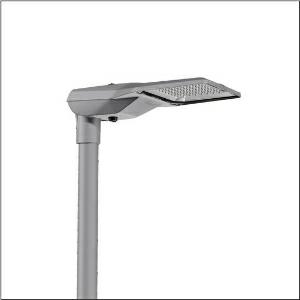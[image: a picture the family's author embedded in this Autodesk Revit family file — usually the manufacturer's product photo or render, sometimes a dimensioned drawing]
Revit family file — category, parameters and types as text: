
# Revit family: streetlight_sl_21_midi___st1_0a_5xe3d33t08mb_6958
name_source: partatom
category: Lighting Fixtures
units: mm (PartAtom-declared; Revit-internal decimal feet)

## family parameters
Cut with Voids When Loaded = No
Host = Face
Light Source = No
Part Type = Normal
Room Calculation Point = No
Round Connector Dimension = Use Diameter
Shared = No

## types (1)
- --- (1 x LED, 18270 lm, 136 W, 3000K)
    Apparent Load = 136 VA
    CIE Flux Codes = 37 72 97 100 100
    Color Rendering = 70
    Color Temperature = 3000K
    Default Elevation = 1800 mm
    Description = Streetlight SL 21 midi, mast luminaire, primary light control with lens, of PMMA, primary optical cover: cover, of toughened safety glass, transparent, light distribution: ST1.0a, light emission: direct distribution, primary light characteristic: asymmetric, installation type: side-entry, post-top, LED, High Power LED, rated luminous flux: 18.270lm, luminous efficacy: 134lm/W, light colour: 730, colour temperature: 3000K, control gear: D4i, control: flexible luminous flux parameterisation, time-dependent luminous flux control, constant luminous flux control, overheat protection, pre-setting: logarithmic dimming characteristic, mains connection: 230..240V, AC, 50/60Hz, start of lifetime: 136W, end of service life: 142W, reduction: 61W, luminaire housing, of diecast aluminium, powder-coated, Siteco® metallic grey (DB 702S), corrosivity category C5 mid according to DIN EN ISO 12944, please order mast flange separately, inclination adjustable: 0°, 5°, 10°, 15°, sealing non-destructively replaceable, multi-level sealing system, length: 644mm, width: 335mm, height: 110mm, mast flange for spigot size: 42mm (side-entry): 5XC10008XM4, 60/48mm (side-entry/post-top): 5XC10108XM2, 76/60mm (side-entry/post-top): 5XC10108XM1, mounting height: 4..8m, Smart Interface below and above, protection rating (complete): IP66, insulation class (complete): insulation class II (safety insulation), certification: CE, ENEC, ENEC+, VDE, impact resistance: IK10, permissible operating ambient temperature for outdoor applications: -40..+50°C, standard-compliant lighting for roads and squares, packaging unit: 1 piece

Light Distribution: ST1.0a
    Height = 111 mm
    Lamp = 1 x LED
    Lamp Light Flux = 18270 lm
    Lamp Power = 136 W
    Lamp count = 1
    Length = 644 mm
    Luminous efficacy = 134 lm/W
    Manufacturer = Siteco
    ModVariant = No
    Model = 5XE3D33T08MB
    Number of Poles = 1
    OnlyDefault = Yes
    Power Factor = 1
    Product Name = Streetlight SL 21 midi | ST1.0a
    Product group = mast luminaire | pylon top
    ProductGroupID = 6100
    Protection Class = Protection class II
    Protection Degree = IP 66
    RLX_Detail_Level = 1
    RLX_Emergency_Light_Flux = 0 lm
    RLX_Emergency_Type = 0
    RLX_Emergency_Type_DB = No
    RlxData = <blob elided: 26953 chars, md5=8f151166>
    Socket = socket
    Standby Power = 0 W
    System Light Flux = 18270 lm
    System Power = 136 W
    Type Comments = factory setting: luminous flux: 100 % | dim-lin: 254 | 695 mA
    Type Image = l_1004304.jpg
    URL = http://relux.com
    VarID = @adj_210567
    Voltage = 0 V
    Weight = 0.00 kg
    Width = 336 mm

## geometry (parser evidence)
native form markers: Blend x4, Sweep x11
no freeform markers — native parametric forms only
